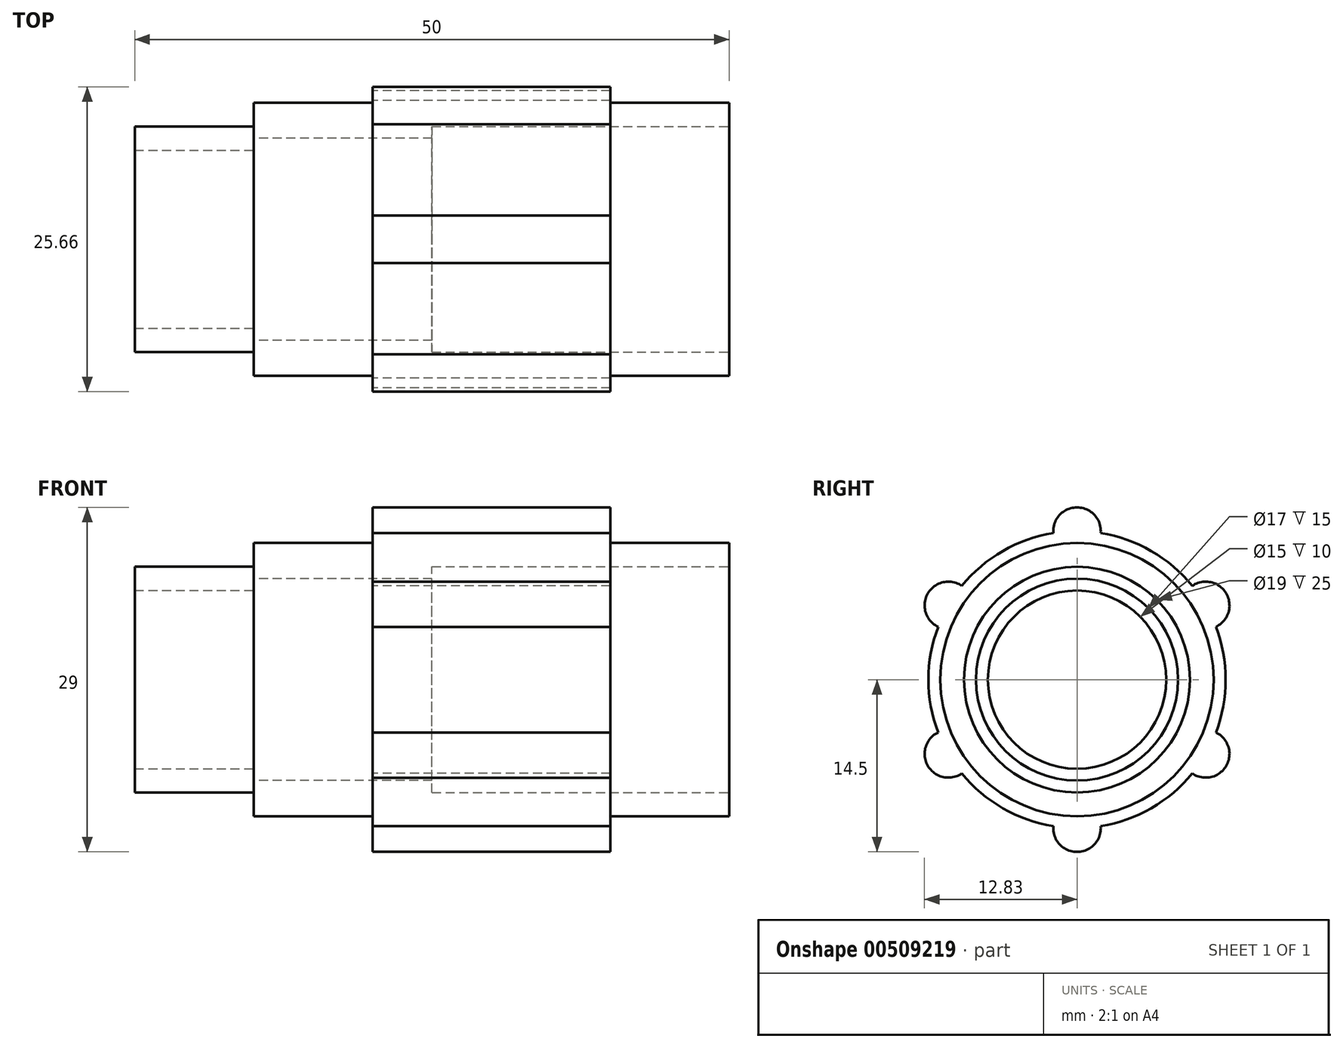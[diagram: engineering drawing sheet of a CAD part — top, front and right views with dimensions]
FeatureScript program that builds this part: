
annotation { "Feature Type Name" : "Feature", "Feature Type Description" : "" }
export const myFeature = defineFeature(function(context is Context, id is Id, definition is map)
    precondition{}
    {
        {
            var Q0;
            Q0=qCreatedBy(makeId("Right.planeOp"),FACE);
            var sketch = newSketch(context, id + "F0", { "sketchPlane" : qUnion([Q0])});
            skCircle(sketch, "E0", {"center": v(0, 0) * mm, "radius": 8.5 * mm});
            skCircle(sketch, "E1", {"center": v(0, 0) * mm, "radius": 12.5 * mm});
            skArc(sketch, "E2", {"start": v(-2, -12.34) * mm, "mid": v(0, -14.5) * mm, "end": v(2, -12.34) * mm});
            skArc(sketch, "E3.1.0", {"start": v(9.69, -7.9) * mm, "mid": v(12.56, -7.25) * mm, "end": v(11.68, -4.44) * mm});
            skArc(sketch, "E3.2.0", {"start": v(11.68, 4.44) * mm, "mid": v(12.56, 7.25) * mm, "end": v(9.69, 7.9) * mm});
            skArc(sketch, "E3.3.0", {"start": v(2, 12.34) * mm, "mid": v(0, 14.5) * mm, "end": v(-2, 12.34) * mm});
            skArc(sketch, "E3.4.0", {"start": v(-9.69, 7.9) * mm, "mid": v(-12.56, 7.25) * mm, "end": v(-11.68, 4.44) * mm});
            skArc(sketch, "E3.5.0", {"start": v(-11.68, -4.44) * mm, "mid": v(-12.56, -7.25) * mm, "end": v(-9.69, -7.9) * mm});
            skSolve(sketch);
        }
        {
            var Q0;
            Q0=qSketchRegion(id+"F0",true);
            extrude(context, id + "F1", {"entities" : qUnion([Q0]), "depth" : 20 * mm, "symmetric" : true});
        }
        {
            var Q0;
            Q0=qCreatedBy(makeId("Right.planeOp"),FACE);
            var sketch = newSketch(context, id + "F2", { "sketchPlane" : qUnion([Q0])});
            skCircle(sketch, "E4", {"center": v(0, 0) * mm, "radius": 8.5 * mm});
            skCircle(sketch, "E5", {"center": v(0, 0) * mm, "radius": 11.5 * mm});
            skSolve(sketch);
        }
        {
            var Q0;
            Q0=qSketchRegion(id+"F2",true);
            extrude(context, id + "F3", {"entities" : qUnion([Q0]), "operationType" : NewBodyOperationType.ADD, "depth" : 40 * mm, "symmetric" : true});
        }
        {
            var Q0;
            Q0=makeQuery(id+"F3.opExtrude","CAP_FACE",FACE,{"disambiguationData":[OSD([sQuery(id+"F2.wireOp",EDGE,"E4"),sQuery(id+"F2.wireOp",EDGE,"E5")])],"isStart":true});
            var sketch = newSketch(context, id + "F4", { "sketchPlane" : qUnion([Q0])});
            skCircle(sketch, "E6", {"center": v(0, 0) * mm, "radius": 9.5 * mm});
            skCircle(sketch, "E7", {"center": v(0, 0) * mm, "radius": 7.5 * mm});
            skSolve(sketch);
        }
        {
            var Q0;
            Q0=qSketchRegion(id+"F4",true);
            extrude(context, id + "F5", {"entities" : qUnion([Q0]), "operationType" : NewBodyOperationType.ADD, "depth" : 10 * mm});
        }
        {
            var Q0;
            Q0=makeQuery(id+"F3.opExtrude","CAP_FACE",FACE,{"disambiguationData":[OSD([sQuery(id+"F2.wireOp",EDGE,"E4"),sQuery(id+"F2.wireOp",EDGE,"E5")])],"isStart":false});
            var sketch = newSketch(context, id + "F6", { "sketchPlane" : qUnion([Q0])});
            skCircle(sketch, "E8", {"center": v(0, 0) * mm, "radius": 9.5 * mm});
            skSolve(sketch);
        }
        {
            var Q0;
            Q0=qSketchRegion(id+"F6",true);
            extrude(context, id + "F7", {"entities" : qUnion([Q0]), "operationType" : NewBodyOperationType.REMOVE, "oppositeDirection" : true, "depth" : 25 * mm});
        }
    });
